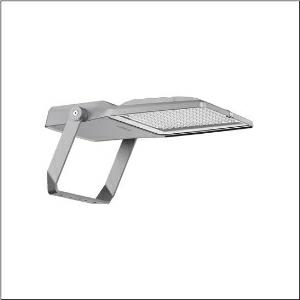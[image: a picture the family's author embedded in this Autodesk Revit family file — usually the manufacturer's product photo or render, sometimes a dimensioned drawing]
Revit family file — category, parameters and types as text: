
# Revit family: floodlight_fl_21_midi___pl52_5xa7786e4d1a_f7a6
name_source: partatom
category: Lighting Fixtures
units: mm (PartAtom-declared; Revit-internal decimal feet)

## family parameters
Cut with Voids When Loaded = No
Host = Face
Light Source = No
Part Type = Normal
Room Calculation Point = No
Round Connector Dimension = Use Diameter
Shared = No

## types (1)
- --- (1 x LED, 28110 lm, 212.4 W, 4000K)
    Apparent Load = 212 VA
    CIE Flux Codes = 26 60 98 100 100
    Color Rendering = 70
    Color Temperature = 4000K
    Default Elevation = 1800 mm
    Description = Floodlight FL 21 midi, floodlight, primary light control with lens, of PMMA, primary optical cover: protective disc, of toughened safety glass, transparent, light distribution: PL52, light emission: direct distribution, installation type: surface-mounted, LED, High Power LED, rated luminous flux: 28.110lm, luminous efficacy: 132lm/W, light colour: 740, colour temperature: 4000K, control gear: Smart Interface (Zhaga)D4i, control: overheat protection, constant luminous flux control, time-dependent luminous flux control, flexible luminous flux parameterisation, pre-setting: logarithmic dimming characteristic, with terminal, 6-pole, mains connection: 220..240V, AC, 50/60Hz, start of lifetime: 212W, end of service life: 231W, reduction: 95W, mounting bracket, of diecast aluminium, powder-coated, SITECO metallic grey (DB 702S), corrosivity category C5 mid according to DIN EN ISO 12944, suitable for swimming pools, chlorine-resistant, sealing non-destructively replaceable, mounting bracket, of steel, galvanised, powder-coated, SITECO metallic grey (DB 702S), Smart Interface below and above, protection rating (complete): IP66, insulation class (complete): insulation class II (safety insulation), certification: CE, ENEC, VDE, protection symbol: D, impact resistance: IK08, permissible operating ambient temperature: -40..+40°C, permissible operating ambient temperature for outdoor applications: -40..+50°C, standard: DIN EN 12944, LABS conformity tested according to VDMA 24364:2018-05, packaging unit: 1 piece

Light Distribution: PL52
    Height = 76 mm
    Lamp = 1 x LED
    Lamp Light Flux = 28110 lm
    Lamp Power = 212.4 W
    Lamp count = 1
    Length = 657 mm
    Luminous efficacy = 132 lm/W
    Manufacturer = Siteco
    ModVariant = No
    Model = 5XA7786E4D1A
    Number of Poles = 1
    OnlyDefault = Yes
    Power Factor = 1
    Product Name = Floodlight FL 21 midi | PL52
    Product group = floodlight | pylon annexe
    ProductGroupID = 6201
    Protection Class = Protection class II
    Protection Degree = IP 66
    RLX_Detail_Level = 1
    RLX_Emergency_Light_Flux = 0 lm
    RLX_Emergency_Type = 0
    RLX_Emergency_Type_DB = No
    RlxData = <blob elided: 101901 chars, md5=2919972b>
    Socket = socket
    Standby Power = 0 W
    System Light Flux = 28110 lm
    System Power = 212 W
    Type Comments = factory setting: luminous flux: 100 % | dim-lin: 254 | 710 mA
    Type Image = l_1006876.jpg
    URL = http://relux.com
    VarID = @adj_093183
    Voltage = 0 V
    Weight = 0.00 kg
    Width = 442 mm

## geometry (parser evidence)
native form markers: Blend x4, Sweep x12
no freeform markers — native parametric forms only
